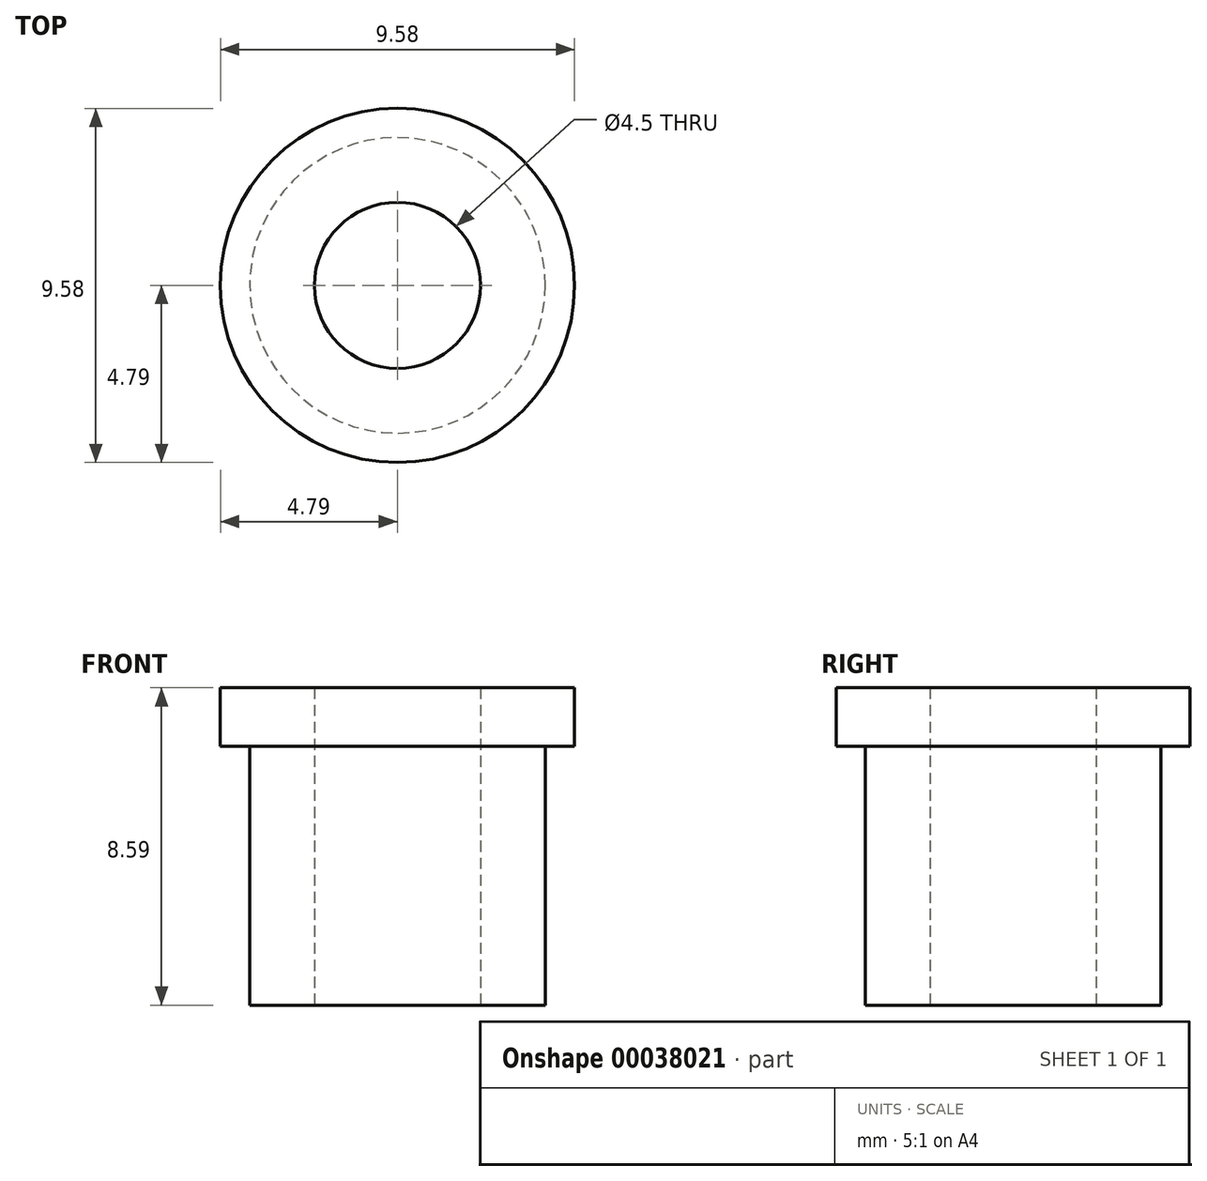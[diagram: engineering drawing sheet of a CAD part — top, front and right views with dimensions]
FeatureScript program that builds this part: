
annotation { "Feature Type Name" : "Feature", "Feature Type Description" : "" }
export const myFeature = defineFeature(function(context is Context, id is Id, definition is map)
    precondition{}
    {
        {
            var Q0;
            Q0=qCreatedBy(makeId("Top.planeOp"),FACE);
            var sketch = newSketch(context, id + "F0", { "sketchPlane" : qUnion([Q0])});
            skCircle(sketch, "E0", {"center": v(0, 0) * mm, "radius": 2.25 * mm});
            skCircle(sketch, "E1", {"center": v(0, 0) * mm, "radius": 4 * mm});
            skSolve(sketch);
        }
        {
            var Q0;
            Q0=qSketchRegion(id+"F0",true);
            extrude(context, id + "F1", {"entities" : qUnion([Q0]), "depth" : 7 * mm});
        }
        {
            var Q0;
            Q0=makeQuery(id+"F1.opExtrude","CAP_FACE",FACE,{"disambiguationData":[OSD([sQuery(id+"F0.wireOp",EDGE,"E0"),sQuery(id+"F0.wireOp",EDGE,"E1")])],"isStart":false});
            var sketch = newSketch(context, id + "F2", { "sketchPlane" : qUnion([Q0])});
            skCircle(sketch, "E2", {"center": v(0, 0) * mm, "radius": 2.25 * mm});
            skCircle(sketch, "E3", {"center": v(0, 0) * mm, "radius": 4.8 * mm});
            skSolve(sketch);
        }
        {
            var Q0;
            Q0=qSketchRegion(id+"F2",true);
            extrude(context, id + "F3", {"entities" : qUnion([Q0]), "operationType" : NewBodyOperationType.ADD, "depth" : 1.59 * mm});
        }
    });
